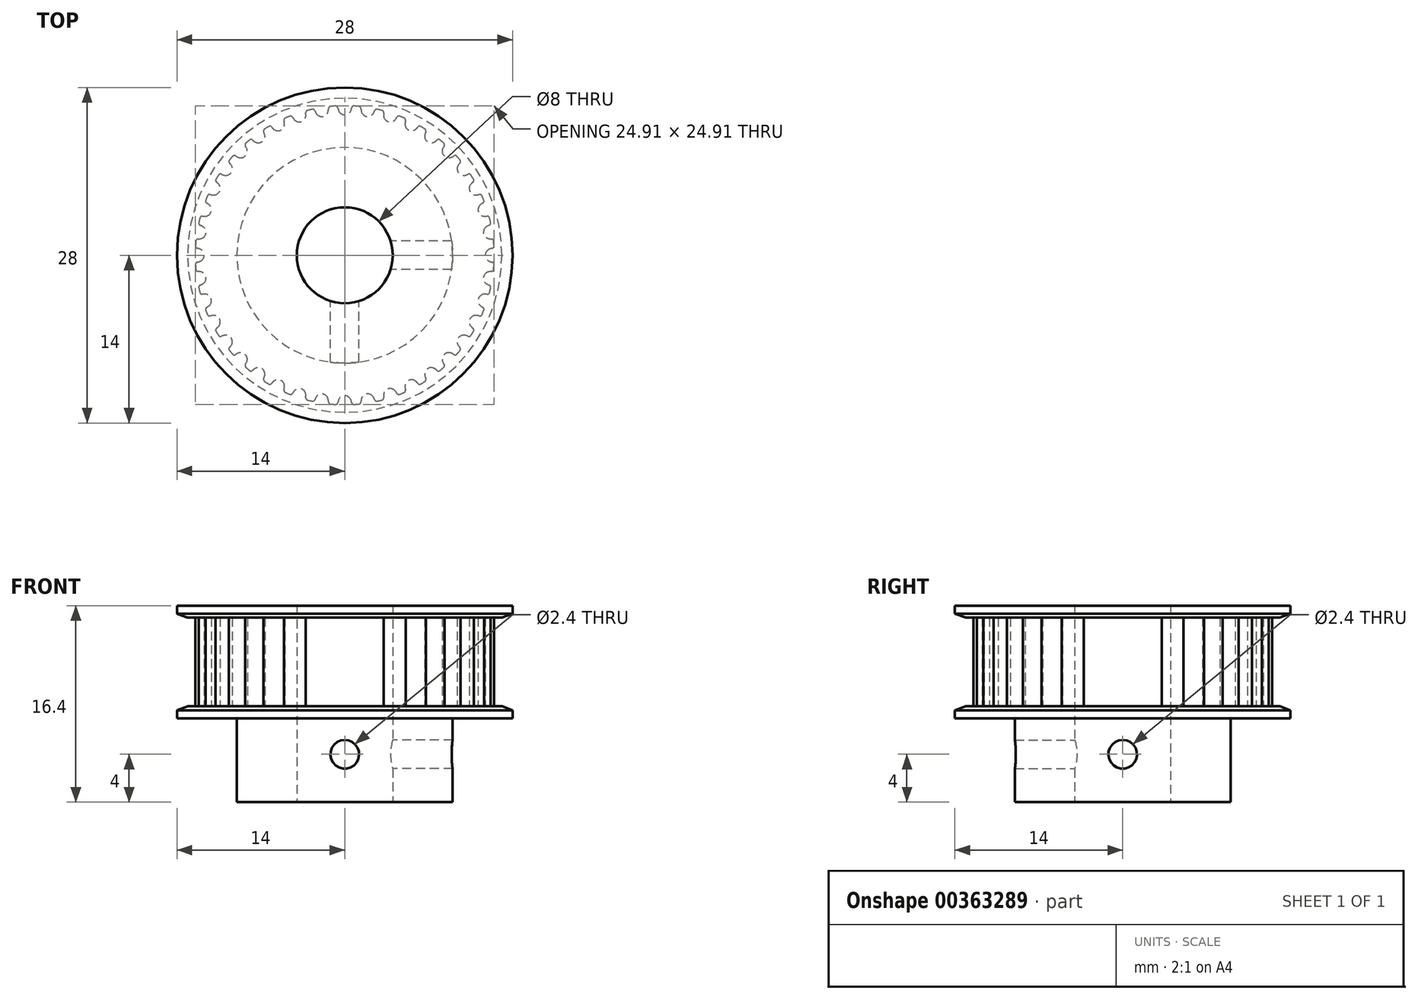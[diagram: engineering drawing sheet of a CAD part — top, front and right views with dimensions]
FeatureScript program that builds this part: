
annotation { "Feature Type Name" : "Feature", "Feature Type Description" : "" }
export const myFeature = defineFeature(function(context is Context, id is Id, definition is map)
    precondition{}
    {
        {
            assignVariable(context, id + "F0", {"name" : "teeth", "anyValue" : 40});
        }
        {
            assignVariable(context, id + "F1", {"name" : "belt_width", "anyValue" : 6 * mm});
        }
        {
            assignVariable(context, id + "F2", {"name" : "bore_diameter", "anyValue" : 8 * mm});
        }
        {
            var Q0;
            Q0=qCreatedBy(makeId("Top.planeOp"),FACE);
            var sketch = newSketch(context, id + "F3", { "sketchPlane" : qUnion([Q0])});
            skLineSegment(sketch, "E0", {"start": v(0, 0) * mm, "end": v(0, 11.73) * mm, "construction": true});
            skCircle(sketch, "E1", {"center": v(0, 0) * mm, "radius": 12.48 * mm});
            skPoint(sketch, "E2.MirrorCS.end.orphan", {"position": v(0.98, 12.44) * mm});
            skLineSegment(sketch, "E3", {"start": v(0.98, 12.44) * mm, "end": v(1, 12.7) * mm, "construction": true});
            skLineSegment(sketch, "E4", {"start": v(-0.98, 12.44) * mm, "end": v(-1, 12.7) * mm, "construction": true});
            skArc(sketch, "E5", {"start": v(0, 11.73) * mm, "mid": v(0.34, 11.84) * mm, "end": v(0.54, 12.14) * mm});
            skArc(sketch, "E6", {"start": v(0.54, 12.14) * mm, "mid": v(0.56, 12.23) * mm, "end": v(0.58, 12.33) * mm, "construction": true});
            skLineSegment(sketch, "E7", {"start": v(0, 11.73) * mm, "end": v(0, 12.48) * mm, "construction": true});
            skLineSegment(sketch, "E8", {"start": v(0, 12.48) * mm, "end": v(0, 12.73) * mm, "construction": true});
            skArc(sketch, "E9", {"start": v(0.58, 12.33) * mm, "mid": v(0.64, 12.42) * mm, "end": v(0.74, 12.46) * mm, "construction": true});
            skArc(sketch, "E10", {"start": v(1, 12.7) * mm, "mid": v(0, 12.73) * mm, "end": v(-1, 12.7) * mm, "construction": true});
            skLineSegment(sketch, "E11", {"start": v(0.98, 12.44) * mm, "end": v(0.92, 11.7) * mm});
            skLineSegment(sketch, "E12", {"start": v(0.92, 11.7) * mm, "end": v(0, 0) * mm});
            skLineSegment(sketch, "E13", {"start": v(0, 0) * mm, "end": v(-0.92, 11.7) * mm});
            skLineSegment(sketch, "E14", {"start": v(-0.92, 11.7) * mm, "end": v(-0.98, 12.44) * mm});
            skArc(sketch, "E15", {"start": v(0.77, 12.45) * mm, "mid": v(0.65, 12.42) * mm, "end": v(0.58, 12.31) * mm});
            skArc(sketch, "E16", {"start": v(0.54, 12.14) * mm, "mid": v(0.56, 12.22) * mm, "end": v(0.58, 12.31) * mm});
            skArc(sketch, "E17.MirrorCS", {"start": v(0, 11.73) * mm, "mid": v(-0.34, 11.84) * mm, "end": v(-0.54, 12.14) * mm});
            skArc(sketch, "E18.MirrorCS", {"start": v(-0.54, 12.14) * mm, "mid": v(-0.56, 12.22) * mm, "end": v(-0.58, 12.31) * mm});
            skArc(sketch, "E19.MirrorCS", {"start": v(-0.77, 12.45) * mm, "mid": v(-0.65, 12.42) * mm, "end": v(-0.58, 12.31) * mm});
            skArc(sketch, "E20", {"start": v(0, 12.48) * mm, "mid": v(-0.2, 12.48) * mm, "end": v(-0.4, 12.47) * mm});
            skArc(sketch, "E21", {"start": v(0.92, 11.7) * mm, "mid": v(0, 11.73) * mm, "end": v(-0.92, 11.7) * mm, "construction": true});
            skLineSegment(sketch, "E22", {"start": v(1, 12.7) * mm, "end": v(1.03, 13.07) * mm, "construction": true});
            skLineSegment(sketch, "E23", {"start": v(-1, 12.7) * mm, "end": v(-1.03, 13.07) * mm, "construction": true});
            skArc(sketch, "E24", {"start": v(-1.03, 13.07) * mm, "mid": v(0, 13.1) * mm, "end": v(1.03, 13.07) * mm, "construction": true});
            skSolve(sketch);
        }
        {
            var Q0;
            Q0=makeQuery(id+"F3.imprint","IMPRINT",FACE,{"disambiguationData":[TD([[makeQuery(id+"F3.imprint","IMPRINT",EDGE,{"derivedFrom":sQuery(id+"F3.wireOp",EDGE,"E5")}),-1.0]])]});
            var Q1;
            {var subQ1=sQuery(id+"F3.wireOp",EDGE,"E14");Q1=makeQuery(id+"F3.imprint","IMPRINT",FACE,{"disambiguationData":[TD([[makeQuery(id+"F3.imprint","IMPRINT",EDGE,{"derivedFrom":subQ1}),-1.0]])]});}
            var Q2;
            {var subQ0=sQuery(id+"F3.wireOp",EDGE,"E12");Q2=makeQuery(id+"F3.imprint","IMPRINT",FACE,{"disambiguationData":[TD([[makeQuery(id+"F3.imprint","IMPRINT",EDGE,{"derivedFrom":subQ0}),-1.0]])]});}
            extrude(context, id + "F4", {"entities" : qUnion([Q0, Q1, Q2]), "endBound" : BoundingType.SYMMETRIC, "depth" : getVariable(context, 'belt_width') + 1.4 * mm});
        }
        {
            var Q0;
            Q0=makeQuery(id+"F4.opExtrude","SWEPT_BODY",BODY,{"disambiguationData":[OSD([sQuery(id+"F3.wireOp",EDGE,"E1"),sQuery(id+"F3.wireOp",EDGE,"E5"),sQuery(id+"F3.wireOp",EDGE,"E11"),sQuery(id+"F3.wireOp",EDGE,"E12"),sQuery(id+"F3.wireOp",EDGE,"E13"),sQuery(id+"F3.wireOp",EDGE,"E14"),sQuery(id+"F3.wireOp",EDGE,"E15"),sQuery(id+"F3.wireOp",EDGE,"E16"),sQuery(id+"F3.wireOp",EDGE,"E17.MirrorCS"),sQuery(id+"F3.wireOp",EDGE,"E18.MirrorCS"),sQuery(id+"F3.wireOp",EDGE,"E19.MirrorCS")])]});
            var Q1;
            Q1=makeQuery(id+"F4.opExtrude","SWEPT_EDGE",EDGE,{"disambiguationData":[OSD([sQuery(id+"F3.wireOp",EDGE,"E12"),sQuery(id+"F3.wireOp",EDGE,"E13")])]});
            circularPattern(context, id + "F5", {"operationType" : NewBodyOperationType.ADD, "entities" : qUnion([Q0]), "axis" : qUnion([Q1]), "angle" : 360 * degree, "instanceCount" : getVariable(context, 'teeth'), "equalSpace" : true});
        }
        {
            var Q0;
            Q0=qCreatedBy(makeId("Front.planeOp"),FACE);
            var sketch = newSketch(context, id + "F6", { "sketchPlane" : qUnion([Q0])});
            skLineSegment(sketch, "E25", {"start": v(0, -3.7) * mm, "end": v(13.1, -3.7) * mm});
            skLineSegment(sketch, "E26", {"start": v(13.1, -3.7) * mm, "end": v(14, -4.02) * mm});
            skLineSegment(sketch, "E27", {"start": v(9, -11.7) * mm, "end": v(0, -11.7) * mm});
            skLineSegment(sketch, "E28", {"start": v(0, 3.7) * mm, "end": v(13.1, 3.7) * mm});
            skLineSegment(sketch, "E29", {"start": v(14, 4.02) * mm, "end": v(13.1, 3.7) * mm});
            skLineSegment(sketch, "E30", {"start": v(14, 4.02) * mm, "end": v(14, 4.7) * mm});
            skLineSegment(sketch, "E31", {"start": v(14, 4.7) * mm, "end": v(0, 4.7) * mm});
            skLineSegment(sketch, "E32", {"start": v(0, 4.7) * mm, "end": v(0, 3.7) * mm});
            skLineSegment(sketch, "E33", {"start": v(13.1, -3.7) * mm, "end": v(14, -3.7) * mm, "construction": true});
            skLineSegment(sketch, "E34", {"start": v(14, -3.7) * mm, "end": v(14, -4.02) * mm, "construction": true});
            skLineSegment(sketch, "E35", {"start": v(13.1, 3.7) * mm, "end": v(14, 3.7) * mm, "construction": true});
            skLineSegment(sketch, "E36", {"start": v(14, 3.7) * mm, "end": v(14, 4.02) * mm, "construction": true});
            skLineSegment(sketch, "E37", {"start": v(12.48, 0) * mm, "end": v(12.48, -3.7) * mm, "construction": true});
            skLineSegment(sketch, "E38", {"start": v(14, -4.7) * mm, "end": v(0, -4.7) * mm});
            skLineSegment(sketch, "E39", {"start": v(14, -4.02) * mm, "end": v(14, -4.7) * mm});
            skLineSegment(sketch, "E40", {"start": v(0, -3.7) * mm, "end": v(0, -4.7) * mm});
            skLineSegment(sketch, "E41", {"start": v(9, -11.7) * mm, "end": v(9, -4.7) * mm});
            skLineSegment(sketch, "E42", {"start": v(0, -11.7) * mm, "end": v(0, -4.7) * mm});
            skSolve(sketch);
        }
        {
            var Q0;
            Q0=makeQuery(id+"F6.imprint","IMPRINT",FACE,{"disambiguationData":[TD([[makeQuery(id+"F6.imprint","IMPRINT",EDGE,{"derivedFrom":sQuery(id+"F6.wireOp",EDGE,"E28")}),1.0]])]});
            var Q1;
            Q1=makeQuery(id+"F6.imprint","IMPRINT",FACE,{"disambiguationData":[TD([[makeQuery(id+"F6.imprint","IMPRINT",EDGE,{"derivedFrom":sQuery(id+"F6.wireOp",EDGE,"E25")}),-1.0]])]});
            var Q2;
            Q2=makeQuery(id+"F6.imprint","IMPRINT",FACE,{"disambiguationData":[TD([[makeQuery(id+"F6.imprint","IMPRINT",EDGE,{"derivedFrom":sQuery(id+"F6.wireOp",EDGE,"E27")}),-1.0]])]});
            var Q3;
            Q3=qConstructionFilter(qBodyType(qCreatedBy(id+"F6",EDGE),BodyType.WIRE),ConstructionObject.NO);
            var Q4;
            Q4=sQuery(id+"F6.wireOp",EDGE,"E42");
            revolve(context, id + "F7", {"operationType" : NewBodyOperationType.ADD, "entities" : qUnion([Q0, Q1, Q2]), "surfaceEntities" : qUnion([Q3]), "axis" : qUnion([Q4]), "revolveType" : RevolveType.FULL});
        }
        {
            var Q0;
            Q0=makeQuery(id+"F7.opRevolve","SWEPT_FACE",FACE,{"disambiguationData":[OSD([sQuery(id+"F6.wireOp",EDGE,"E27")])]});
            var sketch = newSketch(context, id + "F8", { "sketchPlane" : qUnion([Q0])});
            skPoint(sketch, "E43", {"position": v(0, 0) * mm});
            skSolve(sketch);
        }
        {
            var Q0;
            Q0=sQuery(id+"F8.wireOp",VERTEX,"E43");
            var Q1;
            Q1=makeQuery(id+"F4.opExtrude","SWEPT_BODY",BODY,{"disambiguationData":[OSD([sQuery(id+"F3.wireOp",EDGE,"E1"),sQuery(id+"F3.wireOp",EDGE,"E5"),sQuery(id+"F3.wireOp",EDGE,"E11"),sQuery(id+"F3.wireOp",EDGE,"E12"),sQuery(id+"F3.wireOp",EDGE,"E13"),sQuery(id+"F3.wireOp",EDGE,"E14"),sQuery(id+"F3.wireOp",EDGE,"E15"),sQuery(id+"F3.wireOp",EDGE,"E16"),sQuery(id+"F3.wireOp",EDGE,"E17.MirrorCS"),sQuery(id+"F3.wireOp",EDGE,"E18.MirrorCS"),sQuery(id+"F3.wireOp",EDGE,"E19.MirrorCS")])]});
            hole(context, id + "F9", {"style" : HoleStyle.SIMPLE, "holeDiameter" : getVariable(context, 'bore_diameter'), "endStyle" : HoleEndStyle.THROUGH, "locations" : qUnion([Q0]), "scope" : qUnion([Q1]), "isTappedThrough" : true});
        }
        {
            var Q0;
            Q0=qCreatedBy(makeId("Front.planeOp"),FACE);
            var sketch = newSketch(context, id + "F10", { "sketchPlane" : qUnion([Q0])});
            skPoint(sketch, "E44", {"position": v(0, -7.7) * mm});
            skLineSegment(sketch, "E45", {"start": v(0, -11.7) * mm, "end": v(0, -3.7) * mm});
            skSolve(sketch);
        }
        {
            var Q0;
            Q0=qCreatedBy(makeId("Right.planeOp"),FACE);
            var sketch = newSketch(context, id + "F11", { "sketchPlane" : qUnion([Q0])});
            skPoint(sketch, "E46", {"position": v(0, -7.7) * mm});
            skSolve(sketch);
        }
        {
            var Q0;
            Q0=sQuery(id+"F10.wireOp",VERTEX,"E44");
            var Q1;
            Q1=makeQuery(id+"F4.opExtrude","SWEPT_BODY",BODY,{"disambiguationData":[OSD([sQuery(id+"F3.wireOp",EDGE,"E1"),sQuery(id+"F3.wireOp",EDGE,"E5"),sQuery(id+"F3.wireOp",EDGE,"E11"),sQuery(id+"F3.wireOp",EDGE,"E12"),sQuery(id+"F3.wireOp",EDGE,"E13"),sQuery(id+"F3.wireOp",EDGE,"E14"),sQuery(id+"F3.wireOp",EDGE,"E15"),sQuery(id+"F3.wireOp",EDGE,"E16"),sQuery(id+"F3.wireOp",EDGE,"E17.MirrorCS"),sQuery(id+"F3.wireOp",EDGE,"E18.MirrorCS"),sQuery(id+"F3.wireOp",EDGE,"E19.MirrorCS")])]});
            hole(context, id + "F12", {"style" : HoleStyle.SIMPLE, "endStyle" : HoleEndStyle.THROUGH, "oppositeDirection" : true, "standardTappedOrClearance" : lookupTablePath({ "standard" : "ISO", "engagement" : "75%", "pitch" : "0.6 mm", "size" : "M3", "type" : "Tapped" }), "standardBlindInLast" : lookupTablePath({ "standard" : "ISO", "engagement" : "75%", "pitch" : "0.6 mm", "size" : "M3", "type" : "Tapped" }), "holeDiameter" : 2.4 * mm, "locations" : qUnion([Q0]), "scope" : qUnion([Q1]), "isTappedThrough" : true, "showTappedDepth" : true});
        }
        {
            var Q0;
            Q0=sQuery(id+"F11.wireOp",VERTEX,"E46");
            var Q1;
            Q1=makeQuery(id+"F4.opExtrude","SWEPT_BODY",BODY,{"disambiguationData":[OSD([sQuery(id+"F3.wireOp",EDGE,"E1"),sQuery(id+"F3.wireOp",EDGE,"E5"),sQuery(id+"F3.wireOp",EDGE,"E11"),sQuery(id+"F3.wireOp",EDGE,"E12"),sQuery(id+"F3.wireOp",EDGE,"E13"),sQuery(id+"F3.wireOp",EDGE,"E14"),sQuery(id+"F3.wireOp",EDGE,"E15"),sQuery(id+"F3.wireOp",EDGE,"E16"),sQuery(id+"F3.wireOp",EDGE,"E17.MirrorCS"),sQuery(id+"F3.wireOp",EDGE,"E18.MirrorCS"),sQuery(id+"F3.wireOp",EDGE,"E19.MirrorCS")])]});
            hole(context, id + "F13", {"style" : HoleStyle.SIMPLE, "endStyle" : HoleEndStyle.THROUGH, "oppositeDirection" : true, "standardTappedOrClearance" : lookupTablePath({ "standard" : "ISO", "engagement" : "75%", "pitch" : "0.6 mm", "size" : "M3", "type" : "Tapped" }), "standardBlindInLast" : lookupTablePath({ "standard" : "ISO", "engagement" : "75%", "pitch" : "0.6 mm", "size" : "M3", "type" : "Tapped" }), "holeDiameter" : 2.4 * mm, "locations" : qUnion([Q0]), "scope" : qUnion([Q1]), "isTappedThrough" : true, "showTappedDepth" : true});
        }
    });
